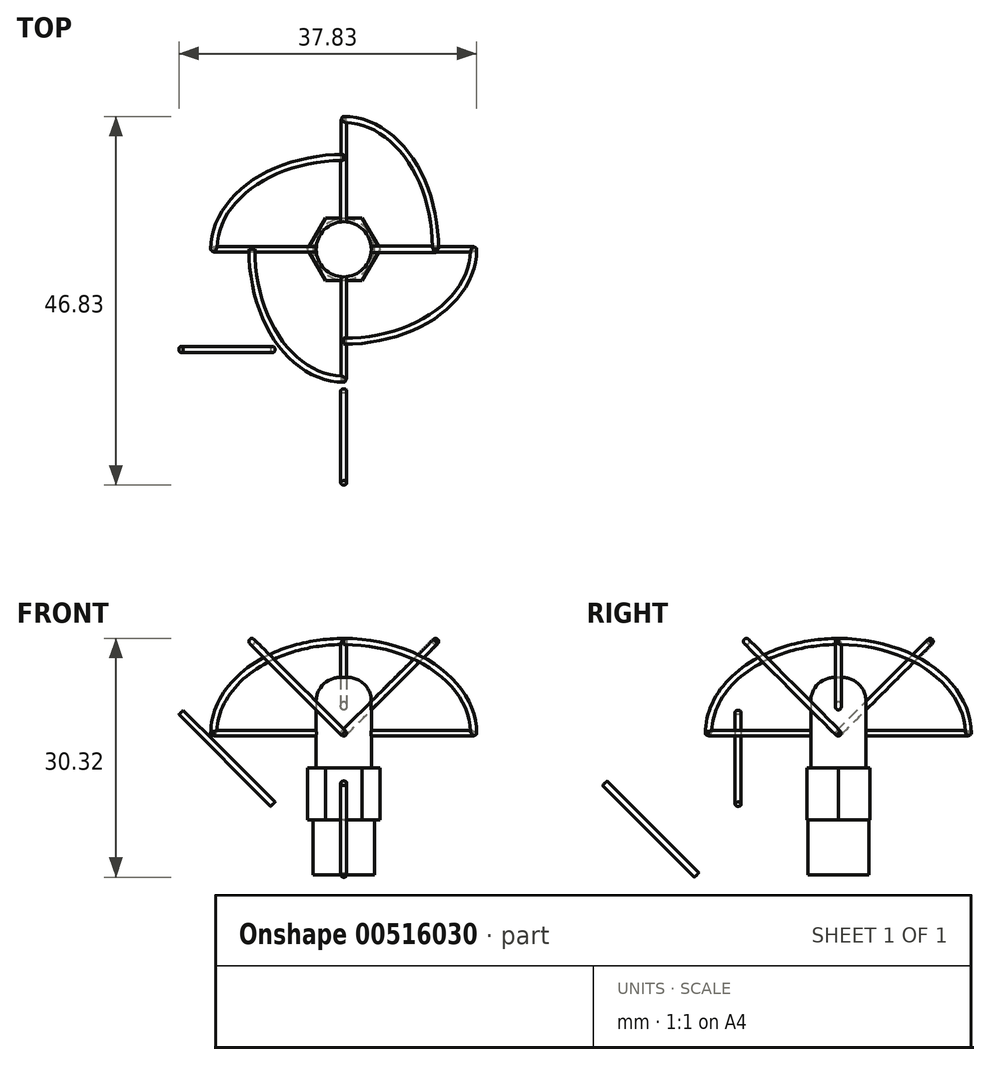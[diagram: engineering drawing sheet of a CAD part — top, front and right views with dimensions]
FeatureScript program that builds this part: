
annotation { "Feature Type Name" : "Feature", "Feature Type Description" : "" }
export const myFeature = defineFeature(function(context is Context, id is Id, definition is map)
    precondition{}
    {
        {
            var Q0;
            Q0=qCreatedBy(makeId("Top.planeOp"),FACE);
            var sketch = newSketch(context, id + "F0", { "sketchPlane" : qUnion([Q0])});
            skCircle(sketch, "E0", {"center": v(0, 0) * mm, "radius": 3.89 * mm});
            skSolve(sketch);
        }
        {
            var Q0;
            Q0 = qSketchRegion(id + "F0", true);
            extrude(context, id + "F1", {"entities" : qUnion([Q0]), "depth" : 7 * mm, "offsetDistance" : 25 * mm});
        }
        {
            var Q0;
            Q0=makeQuery(id+"F1.opExtrude","CAP_FACE",FACE,{"disambiguationData":[OSD([sQuery(id+"F0.wireOp",EDGE,"E0")])],"isStart":false});
            var sketch = newSketch(context, id + "F2", { "sketchPlane" : qUnion([Q0])});
            skCircle(sketch, "E1", {"center": v(0, 0) * mm, "radius": 4.62 * mm, "construction": true});
            skLineSegment(sketch, "E2", {"start": v(-2.3, 4) * mm, "end": v(2.3, 4) * mm});
            skLineSegment(sketch, "E3", {"start": v(2.3, 4) * mm, "end": v(4.62, 0) * mm});
            skLineSegment(sketch, "E4", {"start": v(4.62, 0) * mm, "end": v(2.3, -4) * mm});
            skLineSegment(sketch, "E5", {"start": v(2.3, -4) * mm, "end": v(-2.3, -4) * mm});
            skLineSegment(sketch, "E6", {"start": v(-2.3, -4) * mm, "end": v(-4.62, 0) * mm});
            skLineSegment(sketch, "E7", {"start": v(-4.62, 0) * mm, "end": v(-2.3, 4) * mm});
            skSolve(sketch);
        }
        {
            var Q0;
            Q0 = qSketchRegion(id + "F2", true);
            extrude(context, id + "F3", {"entities" : qUnion([Q0]), "operationType" : NewBodyOperationType.ADD, "depth" : 6.6 * mm, "offsetDistance" : 25 * mm});
        }
        {
            var Q0;
            Q0=makeQuery(id+"F3.opExtrude","CAP_FACE",FACE,{"disambiguationData":[OSD([sQuery(id+"F2.wireOp",EDGE,"E2"),sQuery(id+"F2.wireOp",EDGE,"E3"),sQuery(id+"F2.wireOp",EDGE,"E4"),sQuery(id+"F2.wireOp",EDGE,"E5"),sQuery(id+"F2.wireOp",EDGE,"E6"),sQuery(id+"F2.wireOp",EDGE,"E7")])],"isStart":false});
            var sketch = newSketch(context, id + "F4", { "sketchPlane" : qUnion([Q0])});
            skCircle(sketch, "E8", {"center": v(0, 0) * mm, "radius": 3.5 * mm});
            skSolve(sketch);
        }
        {
            var Q0;
            Q0 = qSketchRegion(id + "F4", true);
            extrude(context, id + "F5", {"entities" : qUnion([Q0]), "operationType" : NewBodyOperationType.ADD, "depth" : 11.5 * mm, "offsetDistance" : 25 * mm});
        }
        {
            var Q0;
            Q0=makeQuery(id+"F5.opExtrude","CAP_EDGE",EDGE,{"disambiguationData":[OSD([sQuery(id+"F4.wireOp",EDGE,"E8")])],"isStart":false});
            fillet(context, id + "F6", {"entities" : qUnion([Q0]), "radius" : 3 * mm, "tangentPropagation" : true, "allowEdgeOverflow" : false});
        }
        {
            var Q0;
            Q0=qCreatedBy(makeId("Front.planeOp"),FACE);
            var sketch = newSketch(context, id + "F7", { "sketchPlane" : qUnion([Q0])});
            skCircle(sketch, "E9", {"center": v(0, 18) * mm, "radius": 0.35 * mm});
            skSolve(sketch);
        }
        {
            var Q0;
            Q0=qCreatedBy(makeId("Right.planeOp"),FACE);
            var sketch = newSketch(context, id + "F8", { "sketchPlane" : qUnion([Q0])});
            skCircle(sketch, "E10", {"center": v(0, 18) * mm, "radius": 0.35 * mm});
            skSolve(sketch);
        }
        {
            var Q0;
            Q0 = qSketchRegion(id + "F7", true);
            extrude(context, id + "F9", {"entities" : qUnion([Q0]), "operationType" : NewBodyOperationType.ADD, "endBound" : BoundingType.SYMMETRIC, "depth" : 33 * mm, "offsetDistance" : 25 * mm});
        }
        {
            var Q0;
            Q0 = qSketchRegion(id + "F8", true);
            extrude(context, id + "F10", {"entities" : qUnion([Q0]), "operationType" : NewBodyOperationType.ADD, "endBound" : BoundingType.SYMMETRIC, "depth" : 33 * mm, "offsetDistance" : 25 * mm});
        }
        {
            var Q0;
            Q0=qCreatedBy(makeId("Top.planeOp"),FACE);
            var Q1;
            Q1=sQuery(id+"F7.wireOp",VERTEX,"E9.center");
            cPlane(context, id + "F11", {"entities" : qUnion([Q0, Q1]), "cplaneType" : CPlaneType.PLANE_POINT, "offset" : 25 * mm, "width" : 150 * mm, "height" : 150 * mm});
        }
        {
            var Q0;
            Q0=qCreatedBy(id+"F11.planeOp",FACE);
            var sketch = newSketch(context, id + "F12", { "sketchPlane" : qUnion([Q0])});
            skLineSegment(sketch, "E11", {"start": v(-19.95, 0) * mm, "end": v(19.42, 0) * mm, "construction": true});
            skSolve(sketch);
        }
        {
            var Q0;
            Q0=sQuery(id+"F12.wireOp",EDGE,"E11");
            var Q1;
            Q1=qCreatedBy(makeId("Front.planeOp"),FACE);
            cPlane(context, id + "F13", {"entities" : qUnion([Q0, Q1]), "cplaneType" : CPlaneType.LINE_ANGLE, "offset" : 25 * mm, "angle" : 45 * degree, "width" : 150 * mm, "height" : 150 * mm});
        }
        {
            var Q0;
            Q0=qCreatedBy(id+"F13.planeOp",FACE);
            var sketch = newSketch(context, id + "F14", { "sketchPlane" : qUnion([Q0])});
            skCircle(sketch, "E12", {"center": v(0, 12.73) * mm, "radius": 0.39 * mm});
            skSolve(sketch);
        }
        {
            var Q0;
            Q0=makeQuery(id+"F14.imprint","IMPRINT",FACE,{"disambiguationData":[TD([[makeQuery(id+"F14.imprint","IMPRINT",EDGE,{"derivedFrom":sQuery(id+"F14.wireOp",EDGE,"E12")}),1.0]])]});
            var Q1;
            Q1=sQuery(id+"F14.wireOp",EDGE,"E12");
            extrude(context, id + "F15", {"entities" : qUnion([Q0]), "surfaceEntities" : qUnion([Q1]), "depth" : (33 / 2) * mm, "offsetDistance" : 25 * mm});
        }
        {
            var Q0;
            Q0=sQuery(id+"F12.wireOp",EDGE,"E11");
            var Q1;
            Q1=qCreatedBy(makeId("Front.planeOp"),FACE);
            cPlane(context, id + "F16", {"entities" : qUnion([Q0, Q1]), "cplaneType" : CPlaneType.LINE_ANGLE, "offset" : 25 * mm, "angle" : 315 * degree, "width" : 150 * mm, "height" : 150 * mm});
        }
        {
            var Q0;
            Q0=qCreatedBy(id+"F16.planeOp",FACE);
            var sketch = newSketch(context, id + "F17", { "sketchPlane" : qUnion([Q0])});
            skCircle(sketch, "E13", {"center": v(0, -12.73) * mm, "radius": 0.39 * mm});
            skSolve(sketch);
        }
        {
            var Q0;
            Q0 = qSketchRegion(id + "F17", true);
            extrude(context, id + "F18", {"entities" : qUnion([Q0]), "operationType" : NewBodyOperationType.ADD, "oppositeDirection" : true, "depth" : (33 / 2) * mm, "offsetDistance" : 25 * mm});
        }
        {
            var Q0;
            Q0=qCreatedBy(makeId("Right.planeOp"),FACE);
            var sketch = newSketch(context, id + "F19", { "sketchPlane" : qUnion([Q0])});
            skLineSegment(sketch, "E14", {"start": v(31.56, 18) * mm, "end": v(-34.95, 18) * mm, "construction": true});
            skSolve(sketch);
        }
        {
            var Q0;
            Q0=sQuery(id+"F19.wireOp",EDGE,"E14");
            var Q1;
            Q1=qCreatedBy(makeId("Right.planeOp"),FACE);
            cPlane(context, id + "F20", {"entities" : qUnion([Q0, Q1]), "cplaneType" : CPlaneType.LINE_ANGLE, "offset" : 25 * mm, "angle" : 315 * degree, "width" : 150 * mm, "height" : 150 * mm});
        }
        {
            var Q0;
            Q0=sQuery(id+"F19.wireOp",EDGE,"E14");
            var Q1;
            Q1=qCreatedBy(makeId("Right.planeOp"),FACE);
            cPlane(context, id + "F21", {"entities" : qUnion([Q0, Q1]), "cplaneType" : CPlaneType.LINE_ANGLE, "offset" : 25 * mm, "angle" : 45 * degree, "width" : 150 * mm, "height" : 150 * mm});
        }
        {
            var Q0;
            Q0=qCreatedBy(id+"F20.planeOp",FACE);
            var sketch = newSketch(context, id + "F22", { "sketchPlane" : qUnion([Q0])});
            skCircle(sketch, "E15", {"center": v(12.73, 0) * mm, "radius": 0.39 * mm});
            skSolve(sketch);
        }
        {
            var Q0;
            Q0 = qSketchRegion(id + "F22", true);
            extrude(context, id + "F23", {"entities" : qUnion([Q0]), "operationType" : NewBodyOperationType.ADD, "depth" : (33 / 2) * mm, "offsetDistance" : 25 * mm});
        }
        {
            var Q0;
            Q0=qCreatedBy(id+"F21.planeOp",FACE);
            var sketch = newSketch(context, id + "F24", { "sketchPlane" : qUnion([Q0])});
            skCircle(sketch, "E16", {"center": v(0, 12.73) * mm, "radius": 0.39 * mm});
            skSolve(sketch);
        }
        {
            var Q0;
            Q0 = qSketchRegion(id + "F24", true);
            extrude(context, id + "F25", {"entities" : qUnion([Q0]), "operationType" : NewBodyOperationType.ADD, "oppositeDirection" : true, "depth" : (33 / 2) * mm, "offsetDistance" : 25 * mm});
        }
        {
            var Q0;
            Q0=qCreatedBy(makeId("Front.planeOp"),FACE);
            var sketch = newSketch(context, id + "F26", { "sketchPlane" : qUnion([Q0])});
            skCircle(sketch, "E17", {"center": v(11.67, 29.67) * mm, "radius": 0.39 * mm});
            skLineSegment(sketch, "E18", {"start": v(20.8, -2.8) * mm, "end": v(-19.48, 37.48) * mm, "construction": true});
            skCircle(sketch, "E19", {"center": v(-11.67, 29.67) * mm, "radius": 0.39 * mm});
            skLineSegment(sketch, "E20", {"start": v(-23.05, -5.05) * mm, "end": v(21.48, 39.48) * mm, "construction": true});
            skSolve(sketch);
        }
        {
            var Q0;
            Q0=makeQuery(id+"F26.imprint","IMPRINT",FACE,{"disambiguationData":[TD([[makeQuery(id+"F26.imprint","IMPRINT",EDGE,{"derivedFrom":sQuery(id+"F26.wireOp",EDGE,"E17")}),1.0]])]});
            var Q1;
            Q1=sQuery(id+"F26.wireOp",EDGE,"E17");
            var Q2;
            Q2=sQuery(id+"F26.wireOp",EDGE,"E18");
            revolve(context, id + "F27", {"operationType" : NewBodyOperationType.ADD, "entities" : qUnion([Q0]), "surfaceEntities" : qUnion([Q1]), "axis" : qUnion([Q2]), "revolveType" : RevolveType.ONE_DIRECTION, "angle" : 90 * degree});
        }
        {
            var Q0;
            Q0=qCreatedBy(makeId("Right.planeOp"),FACE);
            var sketch = newSketch(context, id + "F28", { "sketchPlane" : qUnion([Q0])});
            skCircle(sketch, "E21", {"center": v(11.67, 29.67) * mm, "radius": 0.39 * mm});
            skLineSegment(sketch, "E22", {"start": v(12.73, 5.27) * mm, "end": v(-14.64, 32.64) * mm, "construction": true});
            skCircle(sketch, "E23", {"center": v(-11.67, 29.67) * mm, "radius": 0.39 * mm});
            skLineSegment(sketch, "E24", {"start": v(-16.11, 1.89) * mm, "end": v(17.65, 35.65) * mm, "construction": true});
            skSolve(sketch);
        }
        {
            var Q0;
            Q0=makeQuery(id+"F28.imprint","IMPRINT",FACE,{"disambiguationData":[TD([[makeQuery(id+"F28.imprint","IMPRINT",EDGE,{"derivedFrom":sQuery(id+"F28.wireOp",EDGE,"E23")}),1.0]])]});
            var Q1;
            Q1=sQuery(id+"F28.wireOp",EDGE,"E23");
            var Q2;
            Q2=sQuery(id+"F28.wireOp",EDGE,"E24");
            revolve(context, id + "F29", {"operationType" : NewBodyOperationType.ADD, "entities" : qUnion([Q0]), "surfaceEntities" : qUnion([Q1]), "axis" : qUnion([Q2]), "revolveType" : RevolveType.ONE_DIRECTION, "angle" : 90 * degree});
        }
        {
            var Q0;
            Q0=makeQuery(id+"F28.imprint","IMPRINT",FACE,{"disambiguationData":[TD([[makeQuery(id+"F28.imprint","IMPRINT",EDGE,{"derivedFrom":sQuery(id+"F28.wireOp",EDGE,"E21")}),1.0]])]});
            var Q1;
            Q1=sQuery(id+"F28.wireOp",EDGE,"E21");
            var Q2;
            Q2=sQuery(id+"F28.wireOp",EDGE,"E22");
            revolve(context, id + "F30", {"operationType" : NewBodyOperationType.ADD, "entities" : qUnion([Q0]), "surfaceEntities" : qUnion([Q1]), "axis" : qUnion([Q2]), "revolveType" : RevolveType.ONE_DIRECTION, "angle" : 90 * degree});
        }
        {
            var Q0;
            Q0=makeQuery(id+"F26.imprint","IMPRINT",FACE,{"disambiguationData":[TD([[makeQuery(id+"F26.imprint","IMPRINT",EDGE,{"derivedFrom":sQuery(id+"F26.wireOp",EDGE,"E19")}),1.0]])]});
            var Q1;
            Q1=sQuery(id+"F26.wireOp",EDGE,"E20");
            revolve(context, id + "F31", {"operationType" : NewBodyOperationType.ADD, "entities" : qUnion([Q0]), "axis" : qUnion([Q1]), "revolveType" : RevolveType.ONE_DIRECTION, "angle" : 90 * degree});
        }
    });
